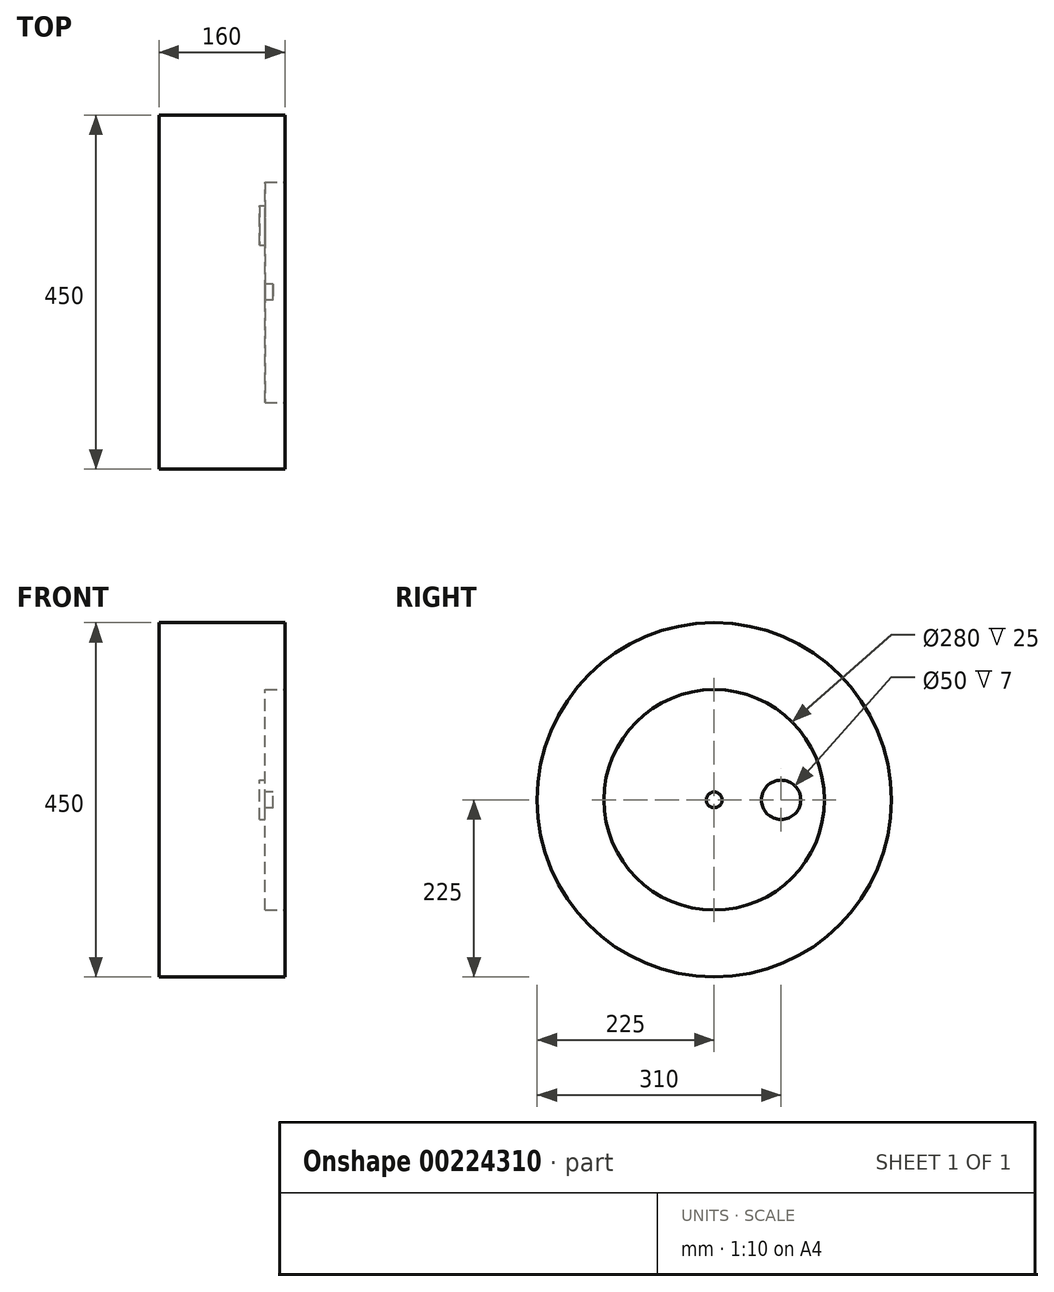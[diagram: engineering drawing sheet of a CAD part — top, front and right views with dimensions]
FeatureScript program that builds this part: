
annotation { "Feature Type Name" : "Feature", "Feature Type Description" : "" }
export const myFeature = defineFeature(function(context is Context, id is Id, definition is map)
    precondition{}
    {
        {
            assignVariable(context, id + "F0", {"name" : "WHEEL_WIDTH", "anyValue" : 160});
        }
        {
            assignVariable(context, id + "F1", {"name" : "WHEEL_HOLE_DEPTH", "anyValue" : 7});
        }
        {
            var Q0;
            Q0=qCreatedBy(makeId("Front.planeOp"),FACE);
            var sketch = newSketch(context, id + "F2", { "sketchPlane" : qUnion([Q0])});
            skLineSegment(sketch, "E0", {"start": v(-215.09, 0) * mm, "end": v(238.4, 0) * mm});
            skSolve(sketch);
        }
        {
            var Q0;
            Q0=qCreatedBy(makeId("Right.planeOp"),FACE);
            var sketch = newSketch(context, id + "F3", { "sketchPlane" : qUnion([Q0])});
            skCircle(sketch, "E1", {"center": v(0, 0) * mm, "radius": 225 * mm});
            skSolve(sketch);
        }
        {
            var Q0;
            Q0=makeQuery(id+"F3.imprint","IMPRINT",FACE,{"disambiguationData":[TD([[makeQuery(id+"F3.imprint","IMPRINT",EDGE,{"derivedFrom":sQuery(id+"F3.wireOp",EDGE,"E1")}),1.0]])]});
            extrude(context, id + "F4", {"entities" : qUnion([Q0]), "depth" : (getVariable(context, 'WHEEL_WIDTH')) * mm});
        }
        {
            var Q0;
            Q0=makeQuery(id+"F4.opExtrude","CAP_FACE",FACE,{"disambiguationData":[OSD([sQuery(id+"F3.wireOp",EDGE,"E1")])],"isStart":false});
            var sketch = newSketch(context, id + "F5", { "sketchPlane" : qUnion([Q0])});
            skCircle(sketch, "E2", {"center": v(0, 0) * mm, "radius": 140 * mm});
            skSolve(sketch);
        }
        {
            var Q0;
            Q0 = qSketchRegion(id + "F5", true);
            extrude(context, id + "F6", {"entities" : qUnion([Q0]), "operationType" : NewBodyOperationType.REMOVE, "oppositeDirection" : true, "depth" : 25 * mm});
        }
        {
            var Q0;
            Q0=makeQuery(id+"F6.boolean.opBoolean","COPY",FACE,{"derivedFrom":makeQuery(id+"F6.opExtrude","CAP_FACE",FACE,{"disambiguationData":[OSD([sQuery(id+"F5.wireOp",EDGE,"E2")])],"isStart":false})});
            var sketch = newSketch(context, id + "F7", { "sketchPlane" : qUnion([Q0])});
            skCircle(sketch, "E3", {"center": v(85, 0) * mm, "radius": 25 * mm});
            skSolve(sketch);
        }
        {
            var Q0;
            Q0=makeQuery(id+"F7.imprint","IMPRINT",FACE,{"disambiguationData":[TD([[makeQuery(id+"F7.imprint","IMPRINT",EDGE,{"derivedFrom":sQuery(id+"F7.wireOp",EDGE,"E3")}),1.0]])]});
            extrude(context, id + "F8", {"entities" : qUnion([Q0]), "operationType" : NewBodyOperationType.REMOVE, "oppositeDirection" : true, "depth" : (getVariable(context, 'WHEEL_HOLE_DEPTH')) * mm});
        }
        {
            var Q0;
            Q0=makeQuery(id+"F6.boolean.opBoolean","COPY",FACE,{"derivedFrom":makeQuery(id+"F6.opExtrude","CAP_FACE",FACE,{"disambiguationData":[OSD([sQuery(id+"F5.wireOp",EDGE,"E2")])],"isStart":false})});
            var sketch = newSketch(context, id + "F9", { "sketchPlane" : qUnion([Q0])});
            skCircle(sketch, "E4", {"center": v(0, 0) * mm, "radius": 10 * mm});
            skSolve(sketch);
        }
        {
            var Q0;
            Q0=makeQuery(id+"F9.imprint","IMPRINT",FACE,{"disambiguationData":[TD([[makeQuery(id+"F9.imprint","IMPRINT",EDGE,{"derivedFrom":sQuery(id+"F9.wireOp",EDGE,"E4")}),1.0]])]});
            var Q1;
            Q1=sQuery(id+"F9.wireOp",EDGE,"E4");
            extrude(context, id + "F10", {"entities" : qUnion([Q0]), "operationType" : NewBodyOperationType.ADD, "surfaceEntities" : qUnion([Q1]), "depth" : 10 * mm});
        }
    });
